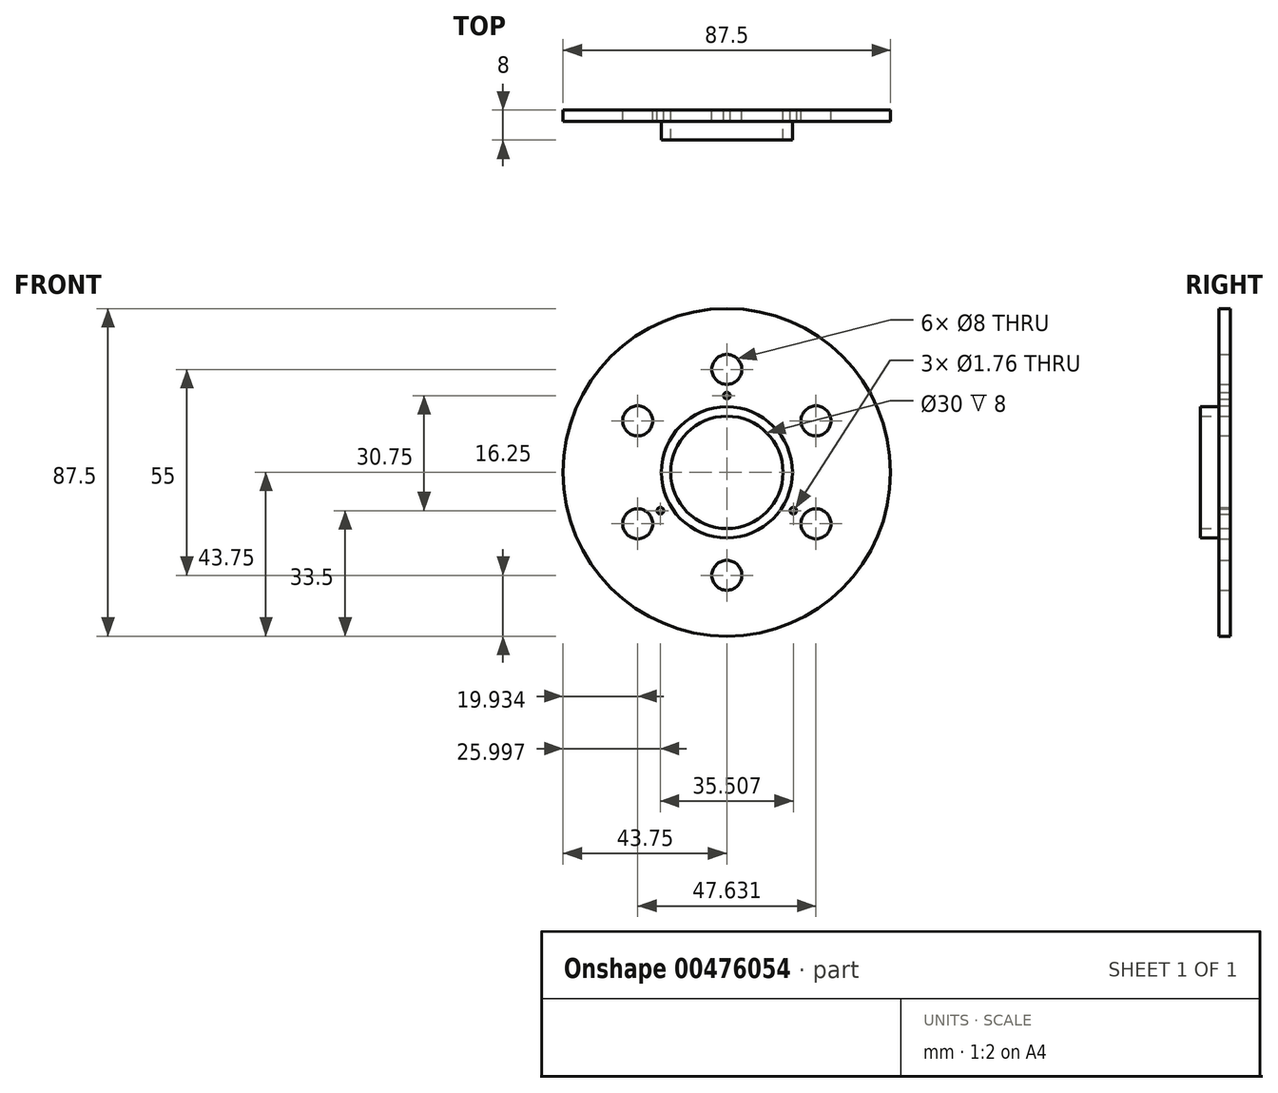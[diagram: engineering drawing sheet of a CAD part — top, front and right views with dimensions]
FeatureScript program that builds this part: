
annotation { "Feature Type Name" : "Feature", "Feature Type Description" : "" }
export const myFeature = defineFeature(function(context is Context, id is Id, definition is map)
    precondition{}
    {
        {
            var Q0;
            Q0=qCreatedBy(makeId("Front.planeOp"),FACE);
            var sketch = newSketch(context, id + "F0", { "sketchPlane" : qUnion([Q0])});
            skCircle(sketch, "E0", {"center": v(0, 0) * mm, "radius": 43.75 * mm});
            skCircle(sketch, "E1", {"center": v(0, 0) * mm, "radius": 15 * mm});
            skCircle(sketch, "E2", {"center": v(0, 0) * mm, "radius": 17.5 * mm});
            skCircle(sketch, "E3", {"center": v(0, 20.5) * mm, "radius": 0.88 * mm});
            skCircle(sketch, "E4.1.0", {"center": v(-17.75, -10.25) * mm, "radius": 0.88 * mm});
            skCircle(sketch, "E4.2.0", {"center": v(17.75, -10.25) * mm, "radius": 0.88 * mm});
            skCircle(sketch, "E5", {"center": v(0, -27.5) * mm, "radius": 4 * mm});
            skCircle(sketch, "E6.1.0", {"center": v(23.82, -13.75) * mm, "radius": 4 * mm});
            skCircle(sketch, "E6.2.0", {"center": v(23.82, 13.75) * mm, "radius": 4 * mm});
            skCircle(sketch, "E6.3.0", {"center": v(0, 27.5) * mm, "radius": 4 * mm});
            skCircle(sketch, "E6.4.0", {"center": v(-23.82, 13.75) * mm, "radius": 4 * mm});
            skCircle(sketch, "E6.5.0", {"center": v(-23.82, -13.75) * mm, "radius": 4 * mm});
            skSolve(sketch);
        }
        {
            var Q0;
            Q0=makeQuery(id+"F0.imprint","IMPRINT",FACE,{"disambiguationData":[TD([[makeQuery(id+"F0.imprint","IMPRINT",EDGE,{"derivedFrom":sQuery(id+"F0.wireOp",EDGE,"E0")}),1.0]])]});
            var Q1;
            Q1=makeQuery(id+"F0.imprint","IMPRINT",FACE,{"disambiguationData":[TD([[makeQuery(id+"F0.imprint","IMPRINT",EDGE,{"derivedFrom":sQuery(id+"F0.wireOp",EDGE,"E1")}),-1.0]])]});
            extrude(context, id + "F1", {"entities" : qUnion([Q0, Q1]), "depth" : 3 * mm});
        }
        {
            var Q0;
            Q0=makeQuery(id+"F0.imprint","IMPRINT",FACE,{"disambiguationData":[TD([[makeQuery(id+"F0.imprint","IMPRINT",EDGE,{"derivedFrom":sQuery(id+"F0.wireOp",EDGE,"E1")}),-1.0]])]});
            extrude(context, id + "F2", {"entities" : qUnion([Q0]), "operationType" : NewBodyOperationType.ADD, "depth" : 8 * mm});
        }
    });
